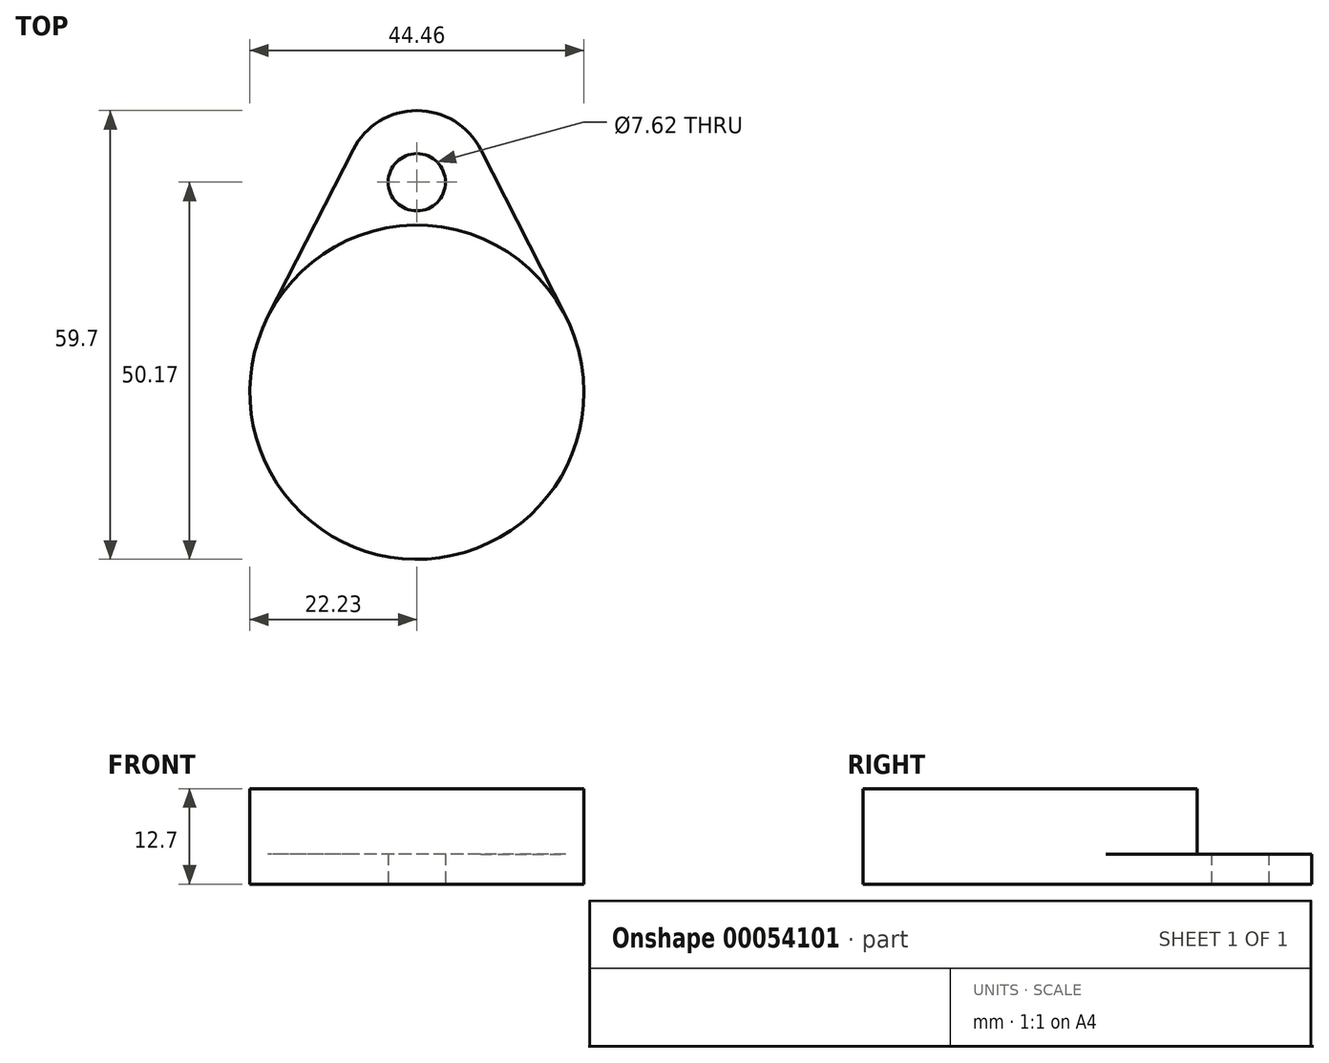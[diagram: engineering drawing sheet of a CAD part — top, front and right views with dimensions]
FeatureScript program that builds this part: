
annotation { "Feature Type Name" : "Feature", "Feature Type Description" : "" }
export const myFeature = defineFeature(function(context is Context, id is Id, definition is map)
    precondition{}
    {
        {
            var Q0;
            Q0=qCreatedBy(makeId("Top.planeOp"),FACE);
            var sketch = newSketch(context, id + "F0", { "sketchPlane" : qUnion([Q0])});
            skCircle(sketch, "E0", {"center": v(0, 0) * mm, "radius": 22.23 * mm});
            skCircle(sketch, "E1", {"center": v(0, 27.94) * mm, "radius": 9.53 * mm});
            skCircle(sketch, "E2", {"center": v(0, 27.94) * mm, "radius": 3.81 * mm});
            skLineSegment(sketch, "E3", {"start": v(-8.48, 32.27) * mm, "end": v(-19.8, 10.1) * mm});
            skLineSegment(sketch, "E4", {"start": v(8.48, 32.27) * mm, "end": v(19.8, 10.1) * mm});
            skSolve(sketch);
        }
        {
            var Q0;
            {var subQ0=sQuery(id+"F0.wireOp",EDGE,"E4");Q0=makeQuery(id+"F0.imprint","IMPRINT",FACE,{"disambiguationData":[TD([[makeQuery(id+"F0.imprint","IMPRINT",EDGE,{"derivedFrom":subQ0}),-1.0]])]});}
            var Q1;
            {var subQ0=sQuery(id+"F0.wireOp",EDGE,"E3");Q1=makeQuery(id+"F0.imprint","IMPRINT",FACE,{"disambiguationData":[TD([[makeQuery(id+"F0.imprint","IMPRINT",EDGE,{"derivedFrom":subQ0}),1.0]])]});}
            var Q2;
            {var subQ0=sQuery(id+"F0.wireOp",EDGE,"E0");var subQ1=makeQuery(id+"F0.imprint","INTERSECT",VERTEX,{"derivedFrom":[subQ0,sQuery(id+"F0.wireOp",EDGE,"E4")]});Q2=makeQuery(id+"F0.imprint","IMPRINT",FACE,{"disambiguationData":[TD([[makeQuery(id+"F0.imprint","IMPRINT",EDGE,{"disambiguationData":[TD([[subQ1,-1.0]])],"derivedFrom":subQ0}),1.0]])]});}
            var Q3;
            Q3=makeQuery(id+"F0.imprint","IMPRINT",FACE,{"disambiguationData":[TD([[makeQuery(id+"F0.imprint","IMPRINT",EDGE,{"derivedFrom":sQuery(id+"F0.wireOp",EDGE,"E2")}),-1.0]])]});
            var Q4;
            {var subQ0=sQuery(id+"F0.wireOp",EDGE,"E1");var subQ1=sQuery(id+"F0.wireOp",EDGE,"E0");var subQ2=makeQuery(id+"F0.imprint","INTERSECT",VERTEX,{"disambiguationData":[OD(0.0)],"derivedFrom":[subQ1,subQ0]});Q4=makeQuery(id+"F0.imprint","IMPRINT",FACE,{"disambiguationData":[TD([[makeQuery(id+"F0.imprint","IMPRINT",EDGE,{"disambiguationData":[TD([[subQ2,-1.0]])],"derivedFrom":subQ1}),1.0]])]});}
            var Q5;
            {var subQ0=sQuery(id+"F0.wireOp",EDGE,"E1");var subQ2=sQuery(id+"F0.wireOp",EDGE,"E0");var subQ7=makeQuery(id+"F0.imprint","INTERSECT",VERTEX,{"disambiguationData":[OD(0.0)],"derivedFrom":[subQ2,subQ0]});Q5=makeQuery(id+"F0.imprint","IMPRINT",FACE,{"disambiguationData":[TD([[makeQuery(id+"F0.imprint","IMPRINT",EDGE,{"disambiguationData":[TD([[subQ7,-1.0]])],"derivedFrom":subQ2}),-1.0]])]});}
            var Q6;
            {var subQ0=sQuery(id+"F0.wireOp",EDGE,"E2");var subQ1=sQuery(id+"F0.wireOp",EDGE,"E0");var subQ2=makeQuery(id+"F0.imprint","INTERSECT",VERTEX,{"disambiguationData":[OD(0.0)],"derivedFrom":[subQ1,subQ0]});Q6=makeQuery(id+"F0.imprint","IMPRINT",FACE,{"disambiguationData":[TD([[makeQuery(id+"F0.imprint","IMPRINT",EDGE,{"disambiguationData":[TD([[subQ2,-1.0]])],"derivedFrom":subQ1}),1.0]])]});}
            extrude(context, id + "F1", {"entities" : qUnion([Q0, Q1, Q2, Q3, Q4, Q5, Q6]), "depth" : 4 * mm});
        }
        {
            var Q0;
            {var subQ0=sQuery(id+"F0.wireOp",EDGE,"E0");var subQ1=makeQuery(id+"F0.imprint","INTERSECT",VERTEX,{"derivedFrom":[subQ0,sQuery(id+"F0.wireOp",EDGE,"E4")]});Q0=makeQuery(id+"F0.imprint","IMPRINT",FACE,{"disambiguationData":[TD([[makeQuery(id+"F0.imprint","IMPRINT",EDGE,{"disambiguationData":[TD([[subQ1,-1.0]])],"derivedFrom":subQ0}),1.0]])]});}
            var Q1;
            {var subQ0=sQuery(id+"F0.wireOp",EDGE,"E1");var subQ1=sQuery(id+"F0.wireOp",EDGE,"E0");var subQ2=makeQuery(id+"F0.imprint","INTERSECT",VERTEX,{"disambiguationData":[OD(0.0)],"derivedFrom":[subQ1,subQ0]});Q1=makeQuery(id+"F0.imprint","IMPRINT",FACE,{"disambiguationData":[TD([[makeQuery(id+"F0.imprint","IMPRINT",EDGE,{"disambiguationData":[TD([[subQ2,-1.0]])],"derivedFrom":subQ1}),1.0]])]});}
            extrude(context, id + "F2", {"entities" : qUnion([Q0, Q1]), "operationType" : NewBodyOperationType.ADD, "depth" : 12.7 * mm});
        }
        {
            var Q0;
            {var subQ0=sQuery(id+"F0.wireOp",EDGE,"E1");var subQ1=sQuery(id+"F0.wireOp",EDGE,"E0");var subQ2=makeQuery(id+"F0.imprint","INTERSECT",VERTEX,{"disambiguationData":[OD(0.0)],"derivedFrom":[subQ1,subQ0]});Q0=makeQuery(id+"F0.imprint","IMPRINT",FACE,{"disambiguationData":[TD([[makeQuery(id+"F0.imprint","IMPRINT",EDGE,{"disambiguationData":[TD([[subQ2,-1.0]])],"derivedFrom":subQ1}),1.0]])]});}
            var Q1;
            {var subQ0=sQuery(id+"F0.wireOp",EDGE,"E0");var subQ1=makeQuery(id+"F0.imprint","INTERSECT",VERTEX,{"derivedFrom":[subQ0,sQuery(id+"F0.wireOp",EDGE,"E4")]});Q1=makeQuery(id+"F0.imprint","IMPRINT",FACE,{"disambiguationData":[TD([[makeQuery(id+"F0.imprint","IMPRINT",EDGE,{"disambiguationData":[TD([[subQ1,-1.0]])],"derivedFrom":subQ0}),1.0]])]});}
            var Q2;
            {var subQ0=sQuery(id+"F0.wireOp",EDGE,"E2");var subQ1=sQuery(id+"F0.wireOp",EDGE,"E0");var subQ2=makeQuery(id+"F0.imprint","INTERSECT",VERTEX,{"disambiguationData":[OD(0.0)],"derivedFrom":[subQ1,subQ0]});Q2=makeQuery(id+"F0.imprint","IMPRINT",FACE,{"disambiguationData":[TD([[makeQuery(id+"F0.imprint","IMPRINT",EDGE,{"disambiguationData":[TD([[subQ2,-1.0]])],"derivedFrom":subQ1}),1.0]])]});}
            extrude(context, id + "F3", {"entities" : qUnion([Q0, Q1, Q2]), "operationType" : NewBodyOperationType.ADD, "depth" : 10 * mm});
        }
    });
